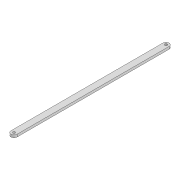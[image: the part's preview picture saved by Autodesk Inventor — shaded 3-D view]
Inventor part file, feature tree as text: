
AUTODESK INVENTOR PART (.ipt)
format: ipt  version: 2022 (Build 260153000, 153)  size: 86,016 bytes
history: native  units: mm
features: extrude x1, sketch x1
ambient origin geometry x8: Origin, YZ Plane, XZ Plane, XY Plane, X Axis, Y Axis, Z Axis, Center Point
bodies: Solid1 (feature_tree)
feature tree (2):
  extrude  "Extrusion1"  Depth=10.0mm
  sketch  "Sketch1"  dims[d0=250.0mm d1=10.0mm d2=4.0mm d3=4.0mm d4=4.0mm d5=0.0mm]
